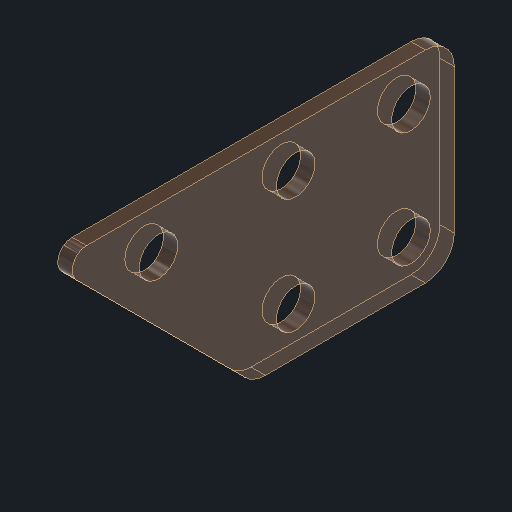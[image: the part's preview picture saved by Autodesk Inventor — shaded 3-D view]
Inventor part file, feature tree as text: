
AUTODESK INVENTOR PART (.ipt)
format: ipt  version: 2024 (Build 280153000, 153)  size: 251,904 bytes
history: native  units: in
note: dims shown in document units (in); Inventor stores cm internally (conversion verified against a paired STEP export)
features: sketch x2, extrude x1, hole x1
ambient origin geometry x8: Origin, YZ Plane, XZ Plane, XY Plane, X Axis, Y Axis, Z Axis, Center Point
bodies: Solid1 (feature_tree)
feature tree (4):
  extrude  "Extrusion1"  Depth=0.125in
  hole  "Hole1"  [1 undecoded]
  sketch  "Sketch1"  dims[d1=0.875in d6=0.125in]
  sketch  "Sketch2"  dims[d7=0.0625in d8=0.0in d13=0.1875in d14=0.5in d15=0.25in d16=0.5in d17=0.167in d18=0.75in d19=0.375in d20=0.25in d21=0.5635in d22=1.0in d23=0.8108in d46=0.0625in d47=0.125in d49=0.188in d50=45.0deg d51=0.403in d52=45.0deg]
note: 1 required parameter value undecoded (feature->parameter linkage not recoverable at this tier; creation-order binding heuristic only, values carry confidence <= 0.55)
